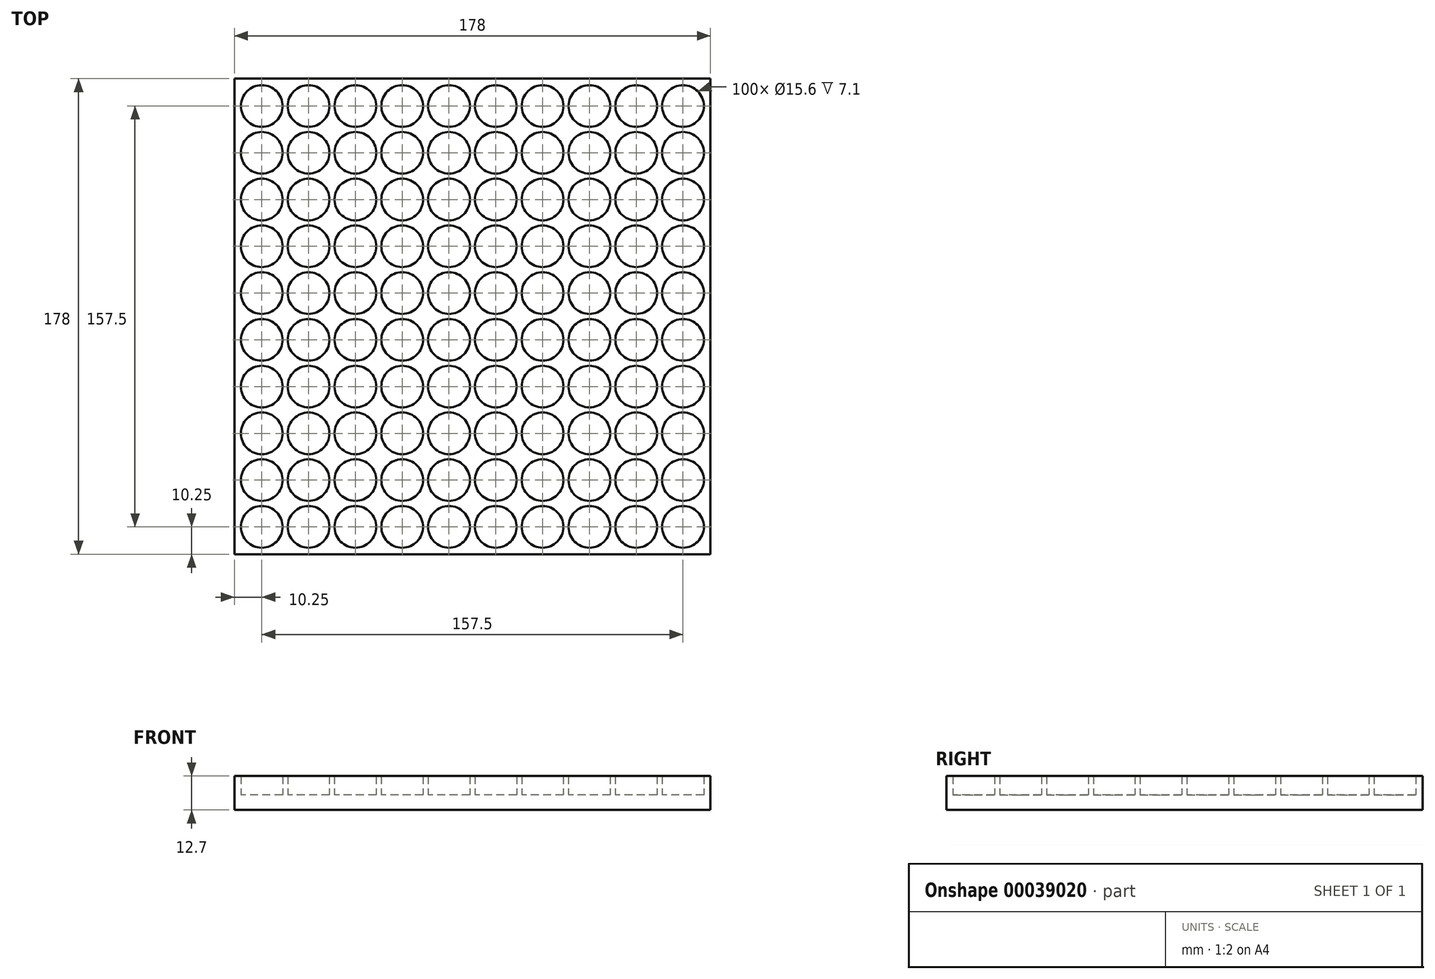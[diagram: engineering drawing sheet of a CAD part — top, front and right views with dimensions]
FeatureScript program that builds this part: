
annotation { "Feature Type Name" : "Feature", "Feature Type Description" : "" }
export const myFeature = defineFeature(function(context is Context, id is Id, definition is map)
    precondition{}
    {
        {
            var Q0;
            Q0=qCreatedBy(makeId("Top.planeOp"),FACE);
            var sketch = newSketch(context, id + "F0", { "sketchPlane" : qUnion([Q0])});
            skCircle(sketch, "E0", {"center": v(0, 0) * mm, "radius": 7.8 * mm});
            skCircle(sketch, "E1.0.1.0", {"center": v(0, 17.5) * mm, "radius": 7.8 * mm});
            skCircle(sketch, "E1.0.2.0", {"center": v(0, 35) * mm, "radius": 7.8 * mm});
            skCircle(sketch, "E1.0.3.0", {"center": v(0, 52.5) * mm, "radius": 7.8 * mm});
            skCircle(sketch, "E1.0.4.0", {"center": v(0, 70) * mm, "radius": 7.8 * mm});
            skCircle(sketch, "E1.0.5.0", {"center": v(0, 87.5) * mm, "radius": 7.8 * mm});
            skCircle(sketch, "E1.0.6.0", {"center": v(0, 105) * mm, "radius": 7.8 * mm});
            skCircle(sketch, "E1.0.7.0", {"center": v(0, 122.5) * mm, "radius": 7.8 * mm});
            skCircle(sketch, "E1.0.8.0", {"center": v(0, 140) * mm, "radius": 7.8 * mm});
            skCircle(sketch, "E1.0.9.0", {"center": v(0, 157.5) * mm, "radius": 7.8 * mm});
            skCircle(sketch, "E1.1.0.0", {"center": v(17.5, 0) * mm, "radius": 7.8 * mm});
            skCircle(sketch, "E1.1.1.0", {"center": v(17.5, 17.5) * mm, "radius": 7.8 * mm});
            skCircle(sketch, "E1.1.2.0", {"center": v(17.5, 35) * mm, "radius": 7.8 * mm});
            skCircle(sketch, "E1.1.3.0", {"center": v(17.5, 52.5) * mm, "radius": 7.8 * mm});
            skCircle(sketch, "E1.1.4.0", {"center": v(17.5, 70) * mm, "radius": 7.8 * mm});
            skCircle(sketch, "E1.1.5.0", {"center": v(17.5, 87.5) * mm, "radius": 7.8 * mm});
            skCircle(sketch, "E1.1.6.0", {"center": v(17.5, 105) * mm, "radius": 7.8 * mm});
            skCircle(sketch, "E1.1.7.0", {"center": v(17.5, 122.5) * mm, "radius": 7.8 * mm});
            skCircle(sketch, "E1.1.8.0", {"center": v(17.5, 140) * mm, "radius": 7.8 * mm});
            skCircle(sketch, "E1.1.9.0", {"center": v(17.5, 157.5) * mm, "radius": 7.8 * mm});
            skCircle(sketch, "E1.2.0.0", {"center": v(35, 0) * mm, "radius": 7.8 * mm});
            skCircle(sketch, "E1.2.1.0", {"center": v(35, 17.5) * mm, "radius": 7.8 * mm});
            skCircle(sketch, "E1.2.2.0", {"center": v(35, 35) * mm, "radius": 7.8 * mm});
            skCircle(sketch, "E1.2.3.0", {"center": v(35, 52.5) * mm, "radius": 7.8 * mm});
            skCircle(sketch, "E1.2.4.0", {"center": v(35, 70) * mm, "radius": 7.8 * mm});
            skCircle(sketch, "E1.2.5.0", {"center": v(35, 87.5) * mm, "radius": 7.8 * mm});
            skCircle(sketch, "E1.2.6.0", {"center": v(35, 105) * mm, "radius": 7.8 * mm});
            skCircle(sketch, "E1.2.7.0", {"center": v(35, 122.5) * mm, "radius": 7.8 * mm});
            skCircle(sketch, "E1.2.8.0", {"center": v(35, 140) * mm, "radius": 7.8 * mm});
            skCircle(sketch, "E1.2.9.0", {"center": v(35, 157.5) * mm, "radius": 7.8 * mm});
            skCircle(sketch, "E1.3.0.0", {"center": v(52.5, 0) * mm, "radius": 7.8 * mm});
            skCircle(sketch, "E1.3.1.0", {"center": v(52.5, 17.5) * mm, "radius": 7.8 * mm});
            skCircle(sketch, "E1.3.2.0", {"center": v(52.5, 35) * mm, "radius": 7.8 * mm});
            skCircle(sketch, "E1.3.3.0", {"center": v(52.5, 52.5) * mm, "radius": 7.8 * mm});
            skCircle(sketch, "E1.3.4.0", {"center": v(52.5, 70) * mm, "radius": 7.8 * mm});
            skCircle(sketch, "E1.3.5.0", {"center": v(52.5, 87.5) * mm, "radius": 7.8 * mm});
            skCircle(sketch, "E1.3.6.0", {"center": v(52.5, 105) * mm, "radius": 7.8 * mm});
            skCircle(sketch, "E1.3.7.0", {"center": v(52.5, 122.5) * mm, "radius": 7.8 * mm});
            skCircle(sketch, "E1.3.8.0", {"center": v(52.5, 140) * mm, "radius": 7.8 * mm});
            skCircle(sketch, "E1.3.9.0", {"center": v(52.5, 157.5) * mm, "radius": 7.8 * mm});
            skCircle(sketch, "E1.4.0.0", {"center": v(70, 0) * mm, "radius": 7.8 * mm});
            skCircle(sketch, "E1.4.1.0", {"center": v(70, 17.5) * mm, "radius": 7.8 * mm});
            skCircle(sketch, "E1.4.2.0", {"center": v(70, 35) * mm, "radius": 7.8 * mm});
            skCircle(sketch, "E1.4.3.0", {"center": v(70, 52.5) * mm, "radius": 7.8 * mm});
            skCircle(sketch, "E1.4.4.0", {"center": v(70, 70) * mm, "radius": 7.8 * mm});
            skCircle(sketch, "E1.4.5.0", {"center": v(70, 87.5) * mm, "radius": 7.8 * mm});
            skCircle(sketch, "E1.4.6.0", {"center": v(70, 105) * mm, "radius": 7.8 * mm});
            skCircle(sketch, "E1.4.7.0", {"center": v(70, 122.5) * mm, "radius": 7.8 * mm});
            skCircle(sketch, "E1.4.8.0", {"center": v(70, 140) * mm, "radius": 7.8 * mm});
            skCircle(sketch, "E1.4.9.0", {"center": v(70, 157.5) * mm, "radius": 7.8 * mm});
            skCircle(sketch, "E1.5.0.0", {"center": v(87.5, 0) * mm, "radius": 7.8 * mm});
            skCircle(sketch, "E1.5.1.0", {"center": v(87.5, 17.5) * mm, "radius": 7.8 * mm});
            skCircle(sketch, "E1.5.2.0", {"center": v(87.5, 35) * mm, "radius": 7.8 * mm});
            skCircle(sketch, "E1.5.3.0", {"center": v(87.5, 52.5) * mm, "radius": 7.8 * mm});
            skCircle(sketch, "E1.5.4.0", {"center": v(87.5, 70) * mm, "radius": 7.8 * mm});
            skCircle(sketch, "E1.5.5.0", {"center": v(87.5, 87.5) * mm, "radius": 7.8 * mm});
            skCircle(sketch, "E1.5.6.0", {"center": v(87.5, 105) * mm, "radius": 7.8 * mm});
            skCircle(sketch, "E1.5.7.0", {"center": v(87.5, 122.5) * mm, "radius": 7.8 * mm});
            skCircle(sketch, "E1.5.8.0", {"center": v(87.5, 140) * mm, "radius": 7.8 * mm});
            skCircle(sketch, "E1.5.9.0", {"center": v(87.5, 157.5) * mm, "radius": 7.8 * mm});
            skCircle(sketch, "E1.6.0.0", {"center": v(105, 0) * mm, "radius": 7.8 * mm});
            skCircle(sketch, "E1.6.1.0", {"center": v(105, 17.5) * mm, "radius": 7.8 * mm});
            skCircle(sketch, "E1.6.2.0", {"center": v(105, 35) * mm, "radius": 7.8 * mm});
            skCircle(sketch, "E1.6.3.0", {"center": v(105, 52.5) * mm, "radius": 7.8 * mm});
            skCircle(sketch, "E1.6.4.0", {"center": v(105, 70) * mm, "radius": 7.8 * mm});
            skCircle(sketch, "E1.6.5.0", {"center": v(105, 87.5) * mm, "radius": 7.8 * mm});
            skCircle(sketch, "E1.6.6.0", {"center": v(105, 105) * mm, "radius": 7.8 * mm});
            skCircle(sketch, "E1.6.7.0", {"center": v(105, 122.5) * mm, "radius": 7.8 * mm});
            skCircle(sketch, "E1.6.8.0", {"center": v(105, 140) * mm, "radius": 7.8 * mm});
            skCircle(sketch, "E1.6.9.0", {"center": v(105, 157.5) * mm, "radius": 7.8 * mm});
            skCircle(sketch, "E1.7.0.0", {"center": v(122.5, 0) * mm, "radius": 7.8 * mm});
            skCircle(sketch, "E1.7.1.0", {"center": v(122.5, 17.5) * mm, "radius": 7.8 * mm});
            skCircle(sketch, "E1.7.2.0", {"center": v(122.5, 35) * mm, "radius": 7.8 * mm});
            skCircle(sketch, "E1.7.3.0", {"center": v(122.5, 52.5) * mm, "radius": 7.8 * mm});
            skCircle(sketch, "E1.7.4.0", {"center": v(122.5, 70) * mm, "radius": 7.8 * mm});
            skCircle(sketch, "E1.7.5.0", {"center": v(122.5, 87.5) * mm, "radius": 7.8 * mm});
            skCircle(sketch, "E1.7.6.0", {"center": v(122.5, 105) * mm, "radius": 7.8 * mm});
            skCircle(sketch, "E1.7.7.0", {"center": v(122.5, 122.5) * mm, "radius": 7.8 * mm});
            skCircle(sketch, "E1.7.8.0", {"center": v(122.5, 140) * mm, "radius": 7.8 * mm});
            skCircle(sketch, "E1.7.9.0", {"center": v(122.5, 157.5) * mm, "radius": 7.8 * mm});
            skCircle(sketch, "E1.8.0.0", {"center": v(140, 0) * mm, "radius": 7.8 * mm});
            skCircle(sketch, "E1.8.1.0", {"center": v(140, 17.5) * mm, "radius": 7.8 * mm});
            skCircle(sketch, "E1.8.2.0", {"center": v(140, 35) * mm, "radius": 7.8 * mm});
            skCircle(sketch, "E1.8.3.0", {"center": v(140, 52.5) * mm, "radius": 7.8 * mm});
            skCircle(sketch, "E1.8.4.0", {"center": v(140, 70) * mm, "radius": 7.8 * mm});
            skCircle(sketch, "E1.8.5.0", {"center": v(140, 87.5) * mm, "radius": 7.8 * mm});
            skCircle(sketch, "E1.8.6.0", {"center": v(140, 105) * mm, "radius": 7.8 * mm});
            skCircle(sketch, "E1.8.7.0", {"center": v(140, 122.5) * mm, "radius": 7.8 * mm});
            skCircle(sketch, "E1.8.8.0", {"center": v(140, 140) * mm, "radius": 7.8 * mm});
            skCircle(sketch, "E1.8.9.0", {"center": v(140, 157.5) * mm, "radius": 7.8 * mm});
            skCircle(sketch, "E1.9.0.0", {"center": v(157.5, 0) * mm, "radius": 7.8 * mm});
            skCircle(sketch, "E1.9.1.0", {"center": v(157.5, 17.5) * mm, "radius": 7.8 * mm});
            skCircle(sketch, "E1.9.2.0", {"center": v(157.5, 35) * mm, "radius": 7.8 * mm});
            skCircle(sketch, "E1.9.3.0", {"center": v(157.5, 52.5) * mm, "radius": 7.8 * mm});
            skCircle(sketch, "E1.9.4.0", {"center": v(157.5, 70) * mm, "radius": 7.8 * mm});
            skCircle(sketch, "E1.9.5.0", {"center": v(157.5, 87.5) * mm, "radius": 7.8 * mm});
            skCircle(sketch, "E1.9.6.0", {"center": v(157.5, 105) * mm, "radius": 7.8 * mm});
            skCircle(sketch, "E1.9.7.0", {"center": v(157.5, 122.5) * mm, "radius": 7.8 * mm});
            skCircle(sketch, "E1.9.8.0", {"center": v(157.5, 140) * mm, "radius": 7.8 * mm});
            skCircle(sketch, "E1.9.9.0", {"center": v(157.5, 157.5) * mm, "radius": 7.8 * mm});
            skLineSegment(sketch, "E1.direction1", {"start": v(0, 0) * mm, "end": v(17.5, 0) * mm, "construction": true});
            skLineSegment(sketch, "E1.direction2", {"start": v(0, 0) * mm, "end": v(0, 17.5) * mm, "construction": true});
            skLineSegment(sketch, "E2", {"start": v(70, 87.5) * mm, "end": v(87.5, 70) * mm, "construction": true});
            skLineSegment(sketch, "E3", {"start": v(87.5, 87.5) * mm, "end": v(70, 70) * mm, "construction": true});
            skLineSegment(sketch, "E4.rect.bottom", {"start": v(167.75, -10.25) * mm, "end": v(-10.25, -10.25) * mm});
            skLineSegment(sketch, "E4.rect.top", {"start": v(167.75, 167.75) * mm, "end": v(-10.25, 167.75) * mm});
            skLineSegment(sketch, "E4.rect.left", {"start": v(167.75, -10.25) * mm, "end": v(167.75, 167.75) * mm});
            skLineSegment(sketch, "E4.rect.right", {"start": v(-10.25, -10.25) * mm, "end": v(-10.25, 167.75) * mm});
            skPoint(sketch, "E4.rect.middle", {"position": v(78.75, 78.75) * mm});
            skSolve(sketch);
        }
        {
            var Q0;
            Q0=makeQuery(id+"F0.imprint","IMPRINT",FACE,{"disambiguationData":[TD([[makeQuery(id+"F0.imprint","IMPRINT",EDGE,{"derivedFrom":sQuery(id+"F0.wireOp",EDGE,"E0")}),-1.0]])]});
            extrude(context, id + "F1", {"entities" : qUnion([Q0]), "depth" : 7.1 * mm});
        }
        {
            var Q0;
            Q0=qCreatedBy(makeId("Top.planeOp"),FACE);
            var sketch = newSketch(context, id + "F2", { "sketchPlane" : qUnion([Q0])});
            skLineSegment(sketch, "E5.0", {"start": v(167.75, -10.25) * mm, "end": v(-10.25, -10.25) * mm});
            skLineSegment(sketch, "E5.1", {"start": v(167.75, -10.25) * mm, "end": v(167.75, 167.75) * mm});
            skLineSegment(sketch, "E5.2", {"start": v(167.75, 167.75) * mm, "end": v(-10.25, 167.75) * mm});
            skLineSegment(sketch, "E5.3", {"start": v(-10.25, -10.25) * mm, "end": v(-10.25, 167.75) * mm});
            skSolve(sketch);
        }
        {
            var Q0;
            Q0=qSketchRegion(id+"F2",true);
            extrude(context, id + "F3", {"entities" : qUnion([Q0]), "operationType" : NewBodyOperationType.ADD, "oppositeDirection" : true, "depth" : 5.6 * mm});
        }
    });
